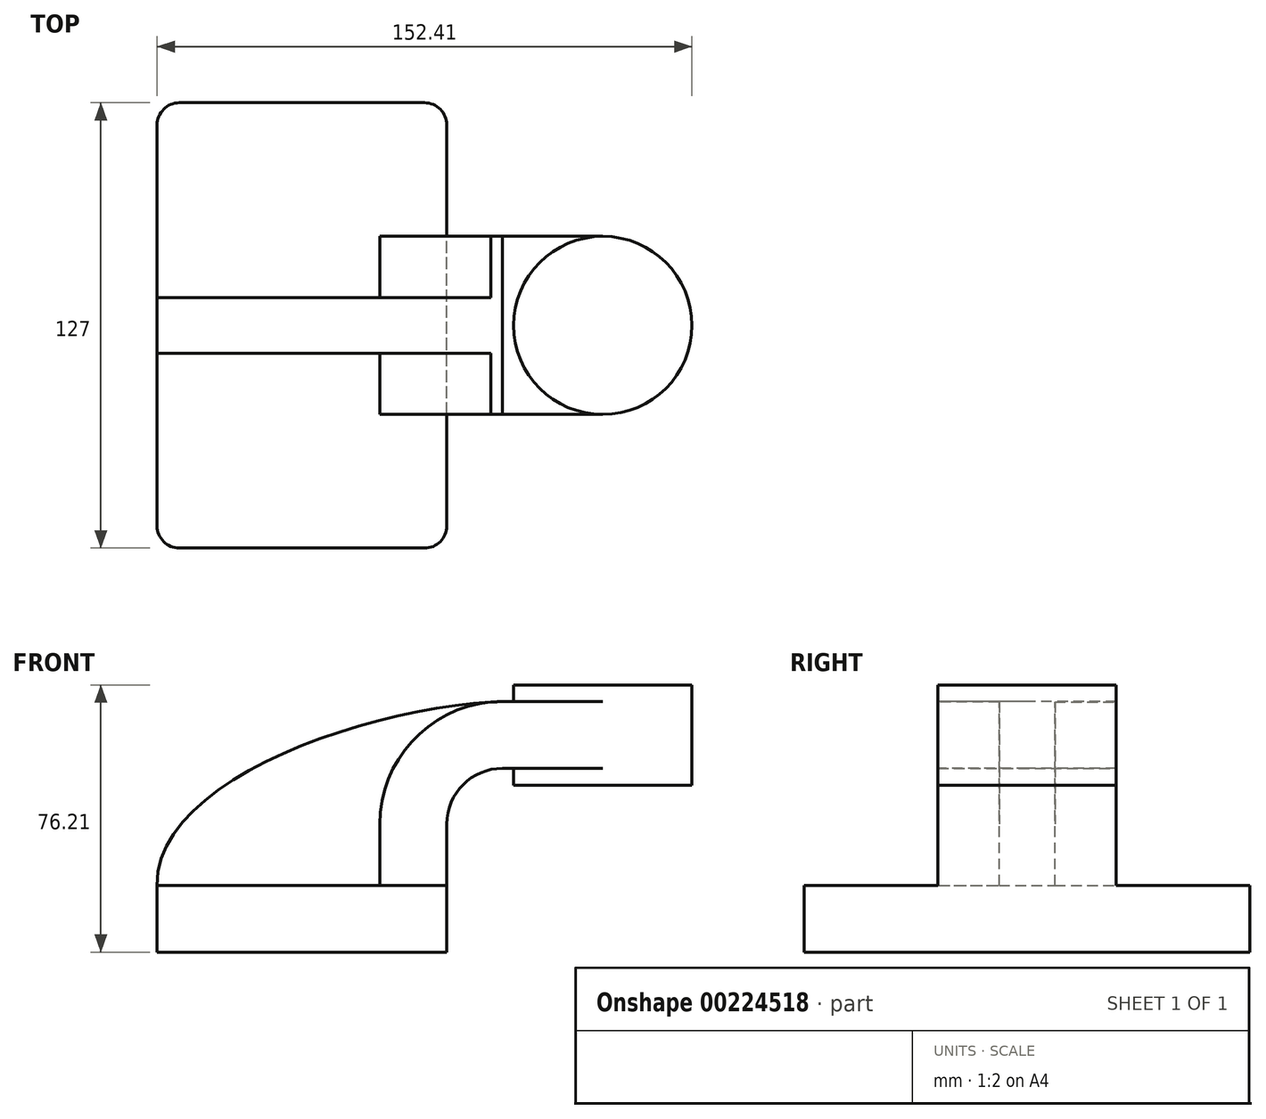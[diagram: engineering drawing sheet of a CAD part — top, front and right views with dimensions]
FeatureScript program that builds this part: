
annotation { "Feature Type Name" : "Feature", "Feature Type Description" : "" }
export const myFeature = defineFeature(function(context is Context, id is Id, definition is map)
    precondition{}
    {
        {
            var Q0;
            Q0=qCreatedBy(makeId("Front.planeOp"),FACE);
            var sketch = newSketch(context, id + "F0", { "sketchPlane" : qUnion([Q0])});
            skLineSegment(sketch, "E0.bottom", {"start": v(-41.28, -9.53) * mm, "end": v(41.28, -9.53) * mm});
            skLineSegment(sketch, "E0.top", {"start": v(-41.28, 9.53) * mm, "end": v(41.28, 9.53) * mm});
            skLineSegment(sketch, "E0.left", {"start": v(-41.27, -9.52) * mm, "end": v(-41.28, 9.53) * mm});
            skLineSegment(sketch, "E0.right", {"start": v(41.28, -9.53) * mm, "end": v(41.27, 9.53) * mm});
            skPoint(sketch, "E0.middle", {"position": v(0, 0) * mm});
            skLineSegment(sketch, "E1.bottom", {"start": v(60.32, 66.67) * mm, "end": v(111.12, 66.67) * mm});
            skLineSegment(sketch, "E1.top", {"start": v(60.32, 38.1) * mm, "end": v(111.12, 38.1) * mm});
            skLineSegment(sketch, "E1.left", {"start": v(60.32, 66.67) * mm, "end": v(60.32, 38.1) * mm});
            skLineSegment(sketch, "E1.right", {"start": v(111.12, 66.67) * mm, "end": v(111.12, 38.1) * mm});
            skPoint(sketch, "E1.middle", {"position": v(85.72, 52.39) * mm});
            skLineSegment(sketch, "E2", {"start": v(41.28, 9.53) * mm, "end": v(41.28, 27) * mm});
            skArc(sketch, "E3", {"start": v(41.28, 27) * mm, "mid": v(45.92, 38.23) * mm, "end": v(57.15, 42.88) * mm});
            skLineSegment(sketch, "E4", {"start": v(57.15, 42.88) * mm, "end": v(85.72, 42.88) * mm});
            skPoint(sketch, "E4.endSnap0", {"position": v(85.72, 38.1) * mm});
            skLineSegment(sketch, "E5.0", {"start": v(57.15, 61.93) * mm, "end": v(85.72, 61.93) * mm});
            skArc(sketch, "E5.1", {"start": v(22.23, 27) * mm, "mid": v(32.45, 51.7) * mm, "end": v(57.15, 61.93) * mm});
            skLineSegment(sketch, "E5.2", {"start": v(22.22, 9.53) * mm, "end": v(22.22, 27) * mm});
            skLineSegment(sketch, "E6", {"start": v(85.72, 38.1) * mm, "end": v(85.72, 66.67) * mm});
            skFitSpline(sketch, "E7", {"points": [v(-41.28, 9.53) * mm, v(57.15, 61.93) * mm], "startDerivative": vector(-1.5, 91.97) * mm, "endDerivative": vector(110.44, 3.74) * mm});
            skSolve(sketch);
        }
        {
            var Q0;
            Q0=makeQuery(id+"F0.imprint","IMPRINT",FACE,{"disambiguationData":[TD([[makeQuery(id+"F0.imprint","IMPRINT",EDGE,{"derivedFrom":sQuery(id+"F0.wireOp",EDGE,"E0.bottom")}),1.0]])]});
            extrude(context, id + "F1", {"entities" : qUnion([Q0]), "depth" : 127 * mm, "symmetric" : true});
        }
        {
            var Q0;
            {var subQ1=sQuery(id+"F0.wireOp",EDGE,"E2");Q0=makeQuery(id+"F0.imprint","IMPRINT",FACE,{"disambiguationData":[TD([[makeQuery(id+"F0.imprint","IMPRINT",EDGE,{"derivedFrom":subQ1}),1.0]])]});}
            var Q1;
            {var subQ0=sQuery(id+"F0.wireOp",EDGE,"E5.0");var subQ1=sQuery(id+"F0.wireOp",EDGE,"E1.left");var subQ2=makeQuery(id+"F0.imprint","INTERSECT",VERTEX,{"derivedFrom":[subQ1,subQ0]});Q1=makeQuery(id+"F0.imprint","IMPRINT",FACE,{"disambiguationData":[TD([[makeQuery(id+"F0.imprint","IMPRINT",EDGE,{"disambiguationData":[TD([[subQ2,-1.0]])],"derivedFrom":subQ1}),1.0]])]});}
            extrude(context, id + "F2", {"entities" : qUnion([Q0, Q1]), "operationType" : NewBodyOperationType.ADD, "depth" : 50.8 * mm, "symmetric" : true});
        }
        {
            var Q0;
            {var subQ3=sQuery(id+"F0.wireOp",EDGE,"E5.2");Q0=makeQuery(id+"F0.imprint","IMPRINT",FACE,{"disambiguationData":[TD([[makeQuery(id+"F0.imprint","IMPRINT",EDGE,{"derivedFrom":subQ3}),1.0]])]});}
            extrude(context, id + "F3", {"entities" : qUnion([Q0]), "operationType" : NewBodyOperationType.ADD, "depth" : 15.88 * mm, "symmetric" : true});
        }
        {
            var Q0;
            {var subQ0=sQuery(id+"F0.wireOp",EDGE,"E1.right");Q0=makeQuery(id+"F0.imprint","IMPRINT",FACE,{"disambiguationData":[TD([[makeQuery(id+"F0.imprint","IMPRINT",EDGE,{"derivedFrom":subQ0}),-1.0]])]});}
            var Q1;
            Q1=sQuery(id+"F0.wireOp",EDGE,"E6");
            revolve(context, id + "F4", {"operationType" : NewBodyOperationType.ADD, "entities" : qUnion([Q0]), "axis" : qUnion([Q1]), "revolveType" : RevolveType.FULL});
        }
        {
            var Q0;
            Q0=makeQuery(id+"F1.opExtrude","CAP_EDGE",EDGE,{"disambiguationData":[OSD([sQuery(id+"F0.wireOp",EDGE,"E0.left")])],"isStart":false});
            var Q1;
            Q1=makeQuery(id+"F1.opExtrude","CAP_EDGE",EDGE,{"disambiguationData":[OSD([sQuery(id+"F0.wireOp",EDGE,"E0.right")])],"isStart":false});
            var Q2;
            Q2=makeQuery(id+"F1.opExtrude","CAP_EDGE",EDGE,{"disambiguationData":[OSD([sQuery(id+"F0.wireOp",EDGE,"E0.left")])],"isStart":true});
            var Q3;
            Q3=makeQuery(id+"F1.opExtrude","CAP_EDGE",EDGE,{"disambiguationData":[OSD([sQuery(id+"F0.wireOp",EDGE,"E0.right")])],"isStart":true});
            fillet(context, id + "F5", {"entities" : qUnion([Q0, Q1, Q2, Q3]), "radius" : 6.35 * mm, "tangentPropagation" : true, "allowEdgeOverflow" : false});
        }
    });
